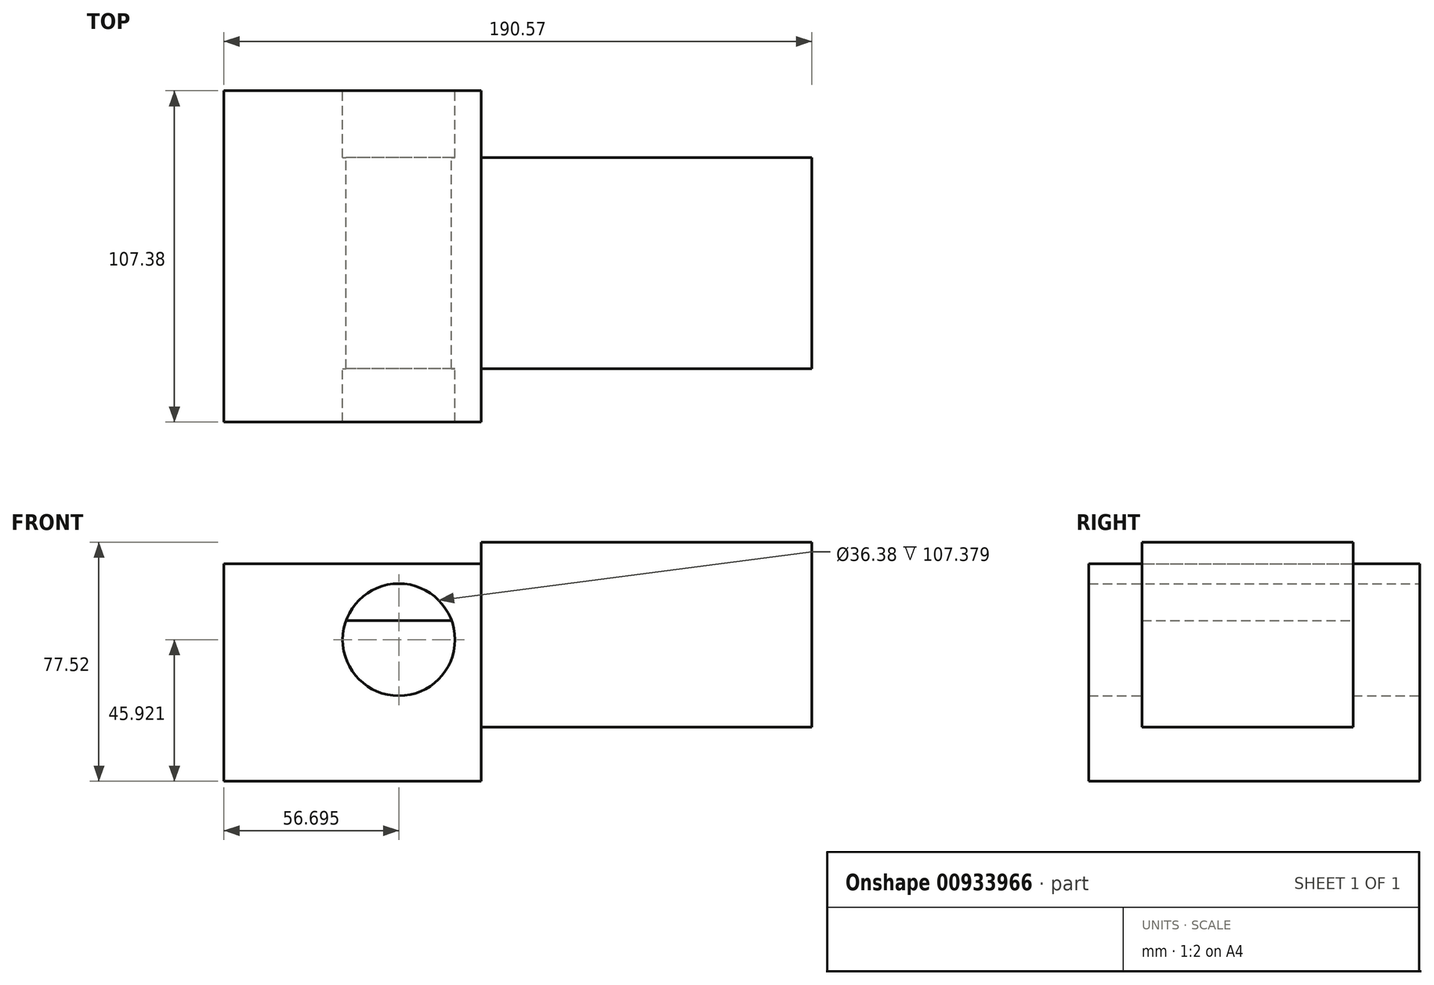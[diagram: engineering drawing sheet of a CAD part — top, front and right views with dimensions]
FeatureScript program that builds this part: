
annotation { "Feature Type Name" : "Feature", "Feature Type Description" : "" }
export const myFeature = defineFeature(function(context is Context, id is Id, definition is map)
    precondition{}
    {
        {
            var Q0;
            Q0=qCreatedBy(makeId("Front.planeOp"),FACE);
            var sketch = newSketch(context, id + "F0", { "sketchPlane" : qUnion([Q0])});
            skLineSegment(sketch, "E0.bottom", {"start": v(-43.47, -33.43) * mm, "end": v(39.92, -33.43) * mm});
            skLineSegment(sketch, "E0.top", {"start": v(-43.47, 37.1) * mm, "end": v(39.92, 37.1) * mm});
            skLineSegment(sketch, "E0.left", {"start": v(-43.47, -33.43) * mm, "end": v(-43.47, 37.1) * mm});
            skLineSegment(sketch, "E0.right", {"start": v(39.92, -33.43) * mm, "end": v(39.92, 37.1) * mm});
            skSolve(sketch);
        }
        {
            var Q0;
            Q0=makeQuery(id+"F0.imprint","IMPRINT",FACE,{"disambiguationData":[TD([[makeQuery(id+"F0.imprint","IMPRINT",EDGE,{"derivedFrom":sQuery(id+"F0.wireOp",EDGE,"E0.bottom")}),1.0]])]});
            var sketch = newSketch(context, id + "F1", { "sketchPlane" : qUnion([Q0])});
            skCircle(sketch, "E1", {"center": v(13.23, 12.5) * mm, "radius": 18.2 * mm});
            skSolve(sketch);
        }
        {
            var Q0;
            Q0=makeQuery(id+"F1.imprint","IMPRINT",FACE,{"disambiguationData":[TD([[makeQuery(id+"F1.imprint","IMPRINT",EDGE,{"derivedFrom":sQuery(id+"F1.wireOp",EDGE,"E1")}),-1.0]])]});
            extrude(context, id + "F2", {"entities" : qUnion([Q0]), "depth" : 107.38 * mm, "offsetDistance" : 25.4 * mm});
        }
        {
            var Q0;
            Q0=makeQuery(id+"F2.opExtrude","SWEPT_FACE",FACE,{"disambiguationData":[OSD([sQuery(id+"F0.wireOp",EDGE,"E0.left")])]});
            var sketch = newSketch(context, id + "F3", { "sketchPlane" : qUnion([Q0])});
            skLineSegment(sketch, "E2.bottom", {"start": v(21.7, 18.69) * mm, "end": v(90.1, 18.69) * mm});
            skLineSegment(sketch, "E2.top", {"start": v(21.7, -15.9) * mm, "end": v(90.1, -15.9) * mm});
            skLineSegment(sketch, "E2.left", {"start": v(21.7, 18.69) * mm, "end": v(21.7, -15.9) * mm});
            skLineSegment(sketch, "E2.right", {"start": v(90.1, 18.69) * mm, "end": v(90.1, -15.9) * mm});
            skSolve(sketch);
        }
        {
            var Q0;
            Q0=makeQuery(id+"F3.imprint","IMPRINT",FACE,{"disambiguationData":[TD([[makeQuery(id+"F3.imprint","IMPRINT",EDGE,{"derivedFrom":sQuery(id+"F3.wireOp",EDGE,"E2.bottom")}),-1.0]])]});
            extrude(context, id + "F4", {"entities" : qUnion([Q0]), "operationType" : NewBodyOperationType.ADD, "oppositeDirection" : true, "depth" : 190.57 * mm, "offsetDistance" : 25.4 * mm});
        }
        {
            var Q0;
            {var subQ2=sQuery(id+"F3.wireOp",EDGE,"E2.bottom");Q0=makeQuery(id+"F4.boolean.opBoolean","SPLIT",FACE,{"disambiguationData":[TD([makeQuery(id+"F2.opExtrude","SWEPT_FACE",FACE,{"disambiguationData":[OSD([sQuery(id+"F0.wireOp",EDGE,"E0.right")])]})])],"derivedFrom":makeQuery(id+"F4.opExtrude","SWEPT_FACE",FACE,{"disambiguationData":[OSD([subQ2])]})});}
            extrude(context, id + "F5", {"entities" : qUnion([Q0]), "operationType" : NewBodyOperationType.ADD, "depth" : 25.4 * mm, "offsetDistance" : 25.4 * mm});
        }
    });
